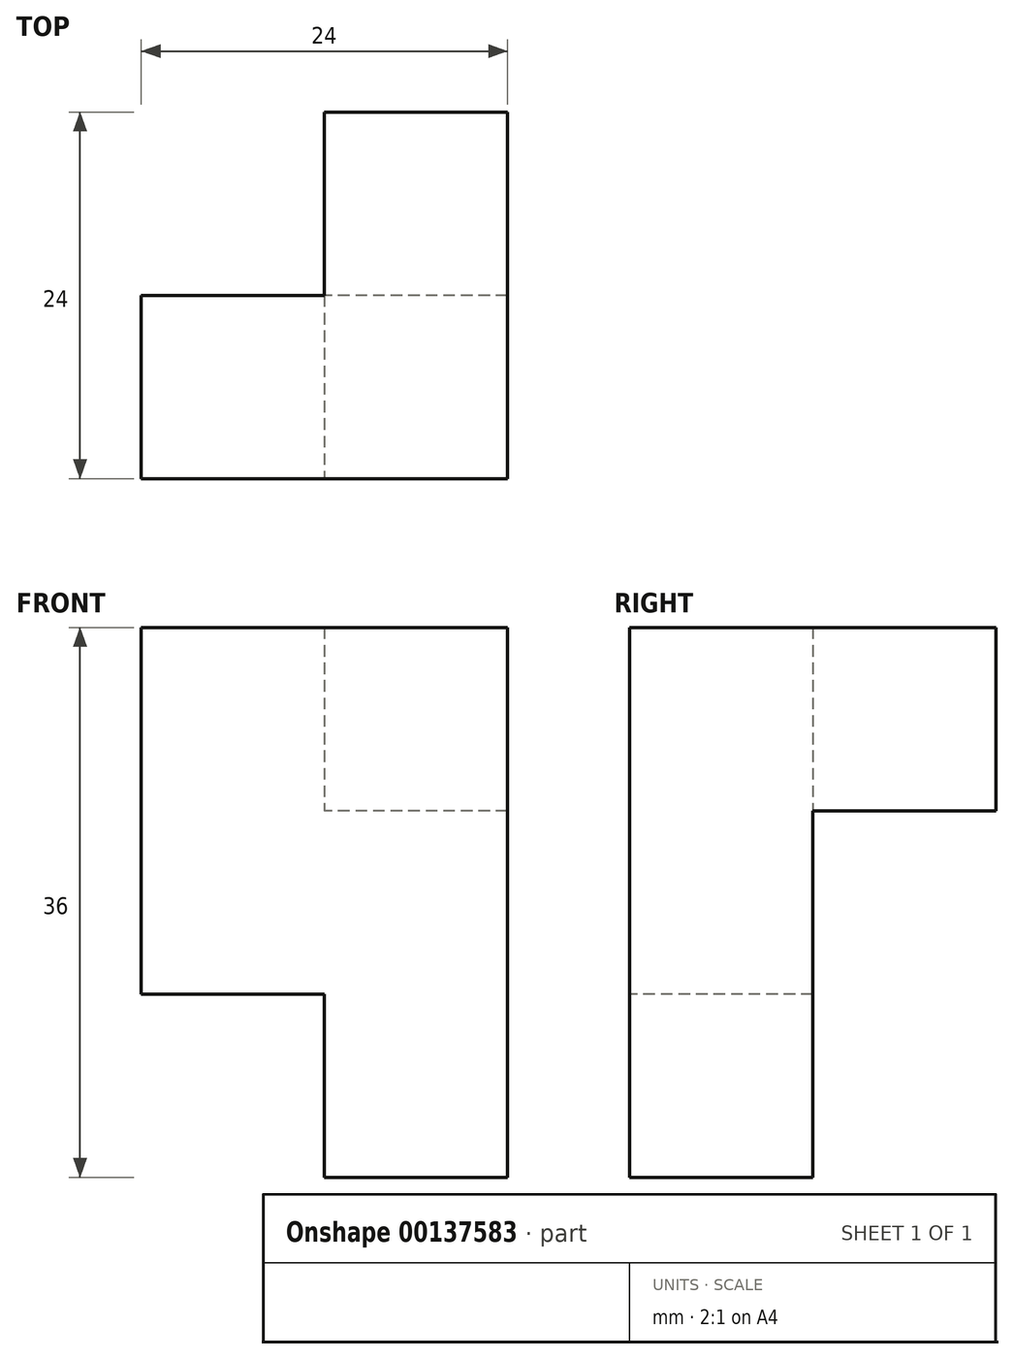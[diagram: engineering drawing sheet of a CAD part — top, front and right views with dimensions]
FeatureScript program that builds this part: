
annotation { "Feature Type Name" : "Feature", "Feature Type Description" : "" }
export const myFeature = defineFeature(function(context is Context, id is Id, definition is map)
    precondition{}
    {
        {
            var Q0;
            Q0=qCreatedBy(makeId("Top.planeOp"),FACE);
            var sketch = newSketch(context, id + "F0", { "sketchPlane" : qUnion([Q0])});
            skLineSegment(sketch, "E0.bottom", {"start": v(-5.33, -32.9) * mm, "end": v(6.67, -32.9) * mm});
            skLineSegment(sketch, "E0.top", {"start": v(-5.33, -44.9) * mm, "end": v(6.67, -44.9) * mm});
            skLineSegment(sketch, "E0.left", {"start": v(-5.33, -32.9) * mm, "end": v(-5.33, -44.9) * mm});
            skLineSegment(sketch, "E0.right", {"start": v(6.67, -32.9) * mm, "end": v(6.67, -44.9) * mm});
            skSolve(sketch);
        }
        {
            var Q0;
            Q0=qSketchRegion(id+"F0",true);
            extrude(context, id + "F1", {"entities" : qUnion([Q0]), "depth" : 12 * mm});
        }
        {
            var Q0;
            Q0=makeQuery(id+"F1.opExtrude","CAP_FACE",FACE,{"disambiguationData":[OSD([sQuery(id+"F0.wireOp",EDGE,"E0.bottom"),sQuery(id+"F0.wireOp",EDGE,"E0.top"),sQuery(id+"F0.wireOp",EDGE,"E0.left"),sQuery(id+"F0.wireOp",EDGE,"E0.right")])],"isStart":false});
            var sketch = newSketch(context, id + "F2", { "sketchPlane" : qUnion([Q0])});
            skLineSegment(sketch, "E1.bottom", {"start": v(-5.33, -32.9) * mm, "end": v(6.67, -32.9) * mm});
            skLineSegment(sketch, "E1.top", {"start": v(-5.33, -44.9) * mm, "end": v(6.67, -44.9) * mm});
            skLineSegment(sketch, "E1.left", {"start": v(-5.33, -32.9) * mm, "end": v(-5.33, -44.9) * mm});
            skLineSegment(sketch, "E1.right", {"start": v(6.67, -32.9) * mm, "end": v(6.67, -44.9) * mm});
            skSolve(sketch);
        }
        {
            var Q0;
            Q0=qSketchRegion(id+"F2",true);
            extrude(context, id + "F3", {"entities" : qUnion([Q0]), "operationType" : NewBodyOperationType.ADD, "depth" : 12 * mm});
        }
        {
            var Q0;
            Q0=makeQuery(id+"F3.opExtrude","CAP_FACE",FACE,{"disambiguationData":[OSD([sQuery(id+"F2.wireOp",EDGE,"E1.bottom"),sQuery(id+"F2.wireOp",EDGE,"E1.top"),sQuery(id+"F2.wireOp",EDGE,"E1.left"),sQuery(id+"F2.wireOp",EDGE,"E1.right")])],"isStart":false});
            var sketch = newSketch(context, id + "F4", { "sketchPlane" : qUnion([Q0])});
            skLineSegment(sketch, "E2.bottom", {"start": v(-5.33, -32.9) * mm, "end": v(6.67, -32.9) * mm});
            skLineSegment(sketch, "E2.top", {"start": v(-5.33, -44.9) * mm, "end": v(6.67, -44.9) * mm});
            skLineSegment(sketch, "E2.left", {"start": v(-5.33, -32.9) * mm, "end": v(-5.33, -44.9) * mm});
            skLineSegment(sketch, "E2.right", {"start": v(6.67, -32.9) * mm, "end": v(6.67, -44.9) * mm});
            skSolve(sketch);
        }
        {
            var Q0;
            Q0=makeQuery(id+"F3.boolean.opBoolean","MERGE",FACE,{"derivedFrom":[makeQuery(id+"F1.opExtrude","SWEPT_FACE",FACE,{"disambiguationData":[OSD([sQuery(id+"F0.wireOp",EDGE,"E0.left")])]}),makeQuery(id+"F3.opExtrude","SWEPT_FACE",FACE,{"disambiguationData":[OSD([sQuery(id+"F2.wireOp",EDGE,"E1.left")])]})]});
            var sketch = newSketch(context, id + "F5", { "sketchPlane" : qUnion([Q0])});
            skLineSegment(sketch, "E3.bottom", {"start": v(32.9, 24) * mm, "end": v(44.9, 24) * mm});
            skLineSegment(sketch, "E3.top", {"start": v(32.9, 12) * mm, "end": v(44.9, 12) * mm});
            skLineSegment(sketch, "E3.left", {"start": v(32.9, 24) * mm, "end": v(32.9, 12) * mm});
            skLineSegment(sketch, "E3.right", {"start": v(44.9, 24) * mm, "end": v(44.9, 12) * mm});
            skSolve(sketch);
        }
        {
            var Q0;
            Q0=qSketchRegion(id+"F5",true);
            extrude(context, id + "F6", {"entities" : qUnion([Q0]), "operationType" : NewBodyOperationType.ADD, "depth" : 12 * mm});
        }
        {
            var Q0;
            Q0=qSketchRegion(id+"F4",true);
            extrude(context, id + "F7", {"entities" : qUnion([Q0]), "operationType" : NewBodyOperationType.ADD, "depth" : 12 * mm});
        }
        {
            var Q0;
            Q0=makeQuery(id+"F6.boolean.opBoolean","MERGE",FACE,{"derivedFrom":[makeQuery(id+"F3.opExtrude","CAP_FACE",FACE,{"disambiguationData":[OSD([sQuery(id+"F2.wireOp",EDGE,"E1.bottom"),sQuery(id+"F2.wireOp",EDGE,"E1.top"),sQuery(id+"F2.wireOp",EDGE,"E1.left"),sQuery(id+"F2.wireOp",EDGE,"E1.right")])],"isStart":false}),makeQuery(id+"F6.opExtrude","SWEPT_FACE",FACE,{"disambiguationData":[OSD([sQuery(id+"F5.wireOp",EDGE,"E3.bottom")])]})]});
            var sketch = newSketch(context, id + "F8", { "sketchPlane" : qUnion([Q0])});
            skLineSegment(sketch, "E4.bottom", {"start": v(-17.33, -32.9) * mm, "end": v(-5.33, -32.9) * mm});
            skLineSegment(sketch, "E4.top", {"start": v(-17.33, -44.9) * mm, "end": v(-5.33, -44.9) * mm});
            skLineSegment(sketch, "E4.left", {"start": v(-17.33, -32.9) * mm, "end": v(-17.33, -44.9) * mm});
            skLineSegment(sketch, "E4.right", {"start": v(-5.33, -32.9) * mm, "end": v(-5.33, -44.9) * mm});
            skSolve(sketch);
        }
        {
            var Q0;
            Q0=qSketchRegion(id+"F8",true);
            extrude(context, id + "F9", {"entities" : qUnion([Q0]), "operationType" : NewBodyOperationType.ADD, "depth" : 12 * mm});
        }
        {
            var Q0;
            Q0=makeQuery(id+"F9.boolean.opBoolean","MERGE",FACE,{"derivedFrom":[makeQuery(id+"F7.boolean.opBoolean","MERGE",FACE,{"derivedFrom":[makeQuery(id+"F6.boolean.opBoolean","MERGE",FACE,{"derivedFrom":[makeQuery(id+"F3.boolean.opBoolean","MERGE",FACE,{"derivedFrom":[makeQuery(id+"F1.opExtrude","SWEPT_FACE",FACE,{"disambiguationData":[OSD([sQuery(id+"F0.wireOp",EDGE,"E0.bottom")])]}),makeQuery(id+"F3.opExtrude","SWEPT_FACE",FACE,{"disambiguationData":[OSD([sQuery(id+"F2.wireOp",EDGE,"E1.bottom")])]})]}),makeQuery(id+"F6.opExtrude","SWEPT_FACE",FACE,{"disambiguationData":[OSD([sQuery(id+"F5.wireOp",EDGE,"E3.left")])]})]}),makeQuery(id+"F7.opExtrude","SWEPT_FACE",FACE,{"disambiguationData":[OSD([sQuery(id+"F4.wireOp",EDGE,"E2.bottom")])]})]}),makeQuery(id+"F9.opExtrude","SWEPT_FACE",FACE,{"disambiguationData":[OSD([sQuery(id+"F8.wireOp",EDGE,"E4.bottom")])]})]});
            var sketch = newSketch(context, id + "F10", { "sketchPlane" : qUnion([Q0])});
            skLineSegment(sketch, "E5.bottom", {"start": v(-6.67, 36) * mm, "end": v(5.33, 36) * mm});
            skLineSegment(sketch, "E5.top", {"start": v(-6.67, 24) * mm, "end": v(5.33, 24) * mm});
            skLineSegment(sketch, "E5.left", {"start": v(-6.67, 36) * mm, "end": v(-6.67, 24) * mm});
            skLineSegment(sketch, "E5.right", {"start": v(5.33, 36) * mm, "end": v(5.33, 24) * mm});
            skSolve(sketch);
        }
        {
            var Q0;
            Q0=qSketchRegion(id+"F10",true);
            extrude(context, id + "F11", {"entities" : qUnion([Q0]), "operationType" : NewBodyOperationType.ADD, "depth" : 12 * mm});
        }
    });
